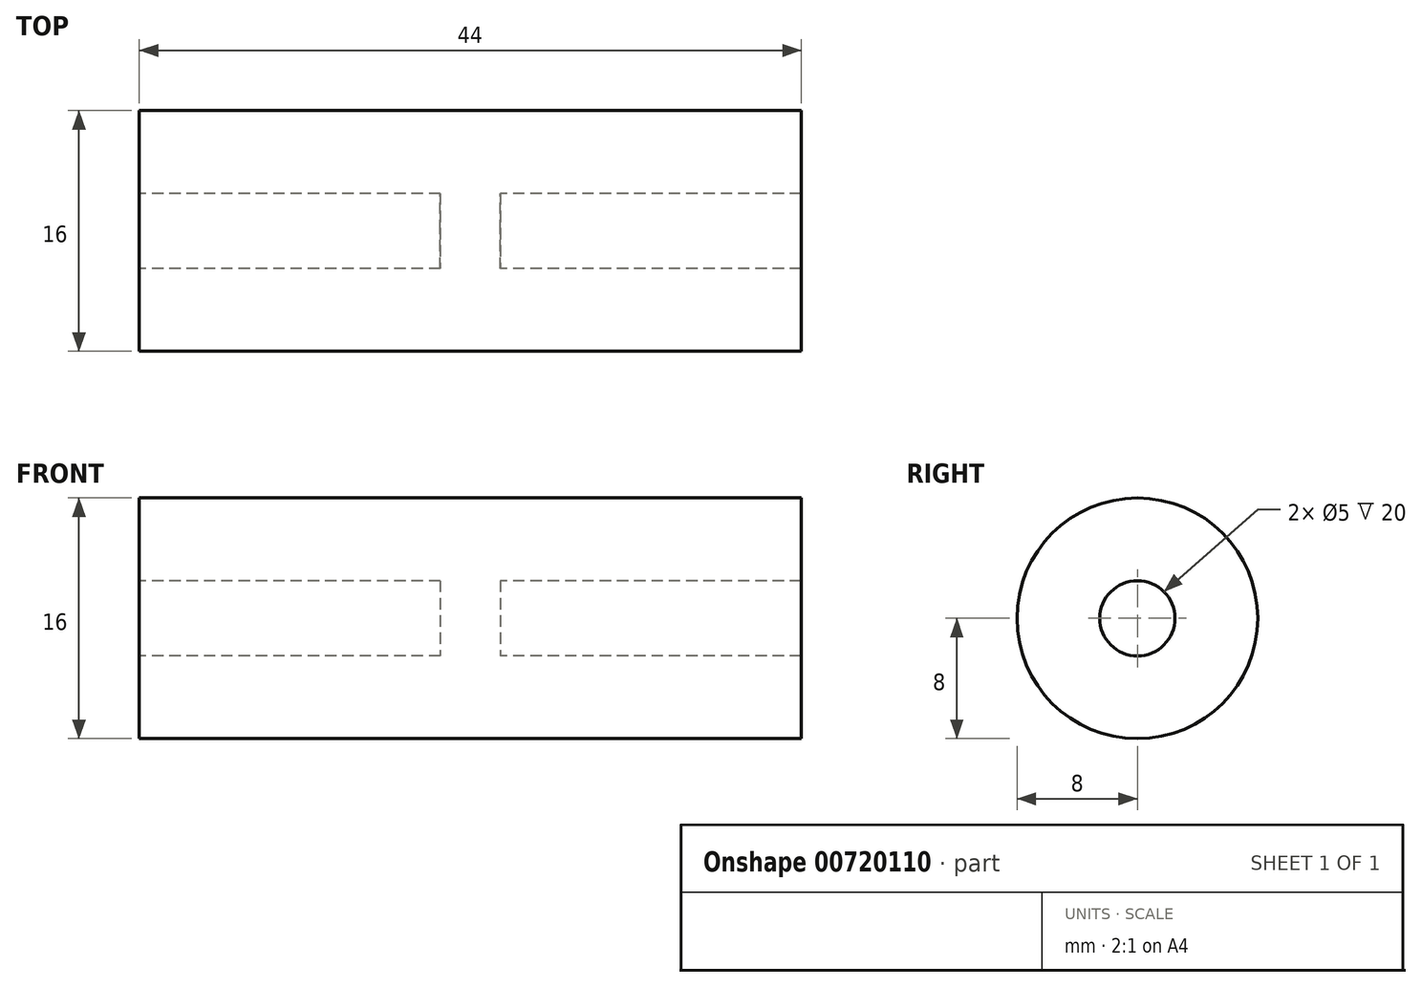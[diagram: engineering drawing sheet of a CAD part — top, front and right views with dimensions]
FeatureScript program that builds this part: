
annotation { "Feature Type Name" : "Feature", "Feature Type Description" : "" }
export const myFeature = defineFeature(function(context is Context, id is Id, definition is map)
    precondition{}
    {
        {
            var Q0;
            Q0=qCreatedBy(makeId("Front.planeOp"),FACE);
            var sketch = newSketch(context, id + "F0", { "sketchPlane" : qUnion([Q0])});
            skLineSegment(sketch, "E0", {"start": v(0, 0) * mm, "end": v(0, 2.5) * mm});
            skLineSegment(sketch, "E1", {"start": v(0, 2.5) * mm, "end": v(20, 2.5) * mm});
            skLineSegment(sketch, "E2", {"start": v(20, 2.5) * mm, "end": v(20, 0) * mm});
            skLineSegment(sketch, "E3", {"start": v(20, 0) * mm, "end": v(24, 0) * mm});
            skLineSegment(sketch, "E4", {"start": v(24, 0) * mm, "end": v(24, 2.5) * mm});
            skLineSegment(sketch, "E5", {"start": v(24, 2.5) * mm, "end": v(44, 2.5) * mm});
            skLineSegment(sketch, "E6", {"start": v(44, 2.5) * mm, "end": v(44, 8) * mm});
            skLineSegment(sketch, "E7", {"start": v(44, 8) * mm, "end": v(0, 8) * mm});
            skLineSegment(sketch, "E8", {"start": v(0, 8) * mm, "end": v(0, 2.5) * mm});
            skSolve(sketch);
        }
        {
            var Q0;
            Q0=makeQuery(id+"F0.imprint","IMPRINT",FACE,{"disambiguationData":[TD([[makeQuery(id+"F0.imprint","IMPRINT",EDGE,{"derivedFrom":sQuery(id+"F0.wireOp",EDGE,"E1")}),1.0]])]});
            var Q1;
            Q1=sQuery(id+"F0.wireOp",EDGE,"E3");
            revolve(context, id + "F1", {"surfaceOperationType" : NewSurfaceOperationType.NEW, "entities" : qUnion([Q0]), "axis" : qUnion([Q1]), "revolveType" : RevolveType.FULL});
        }
    });
